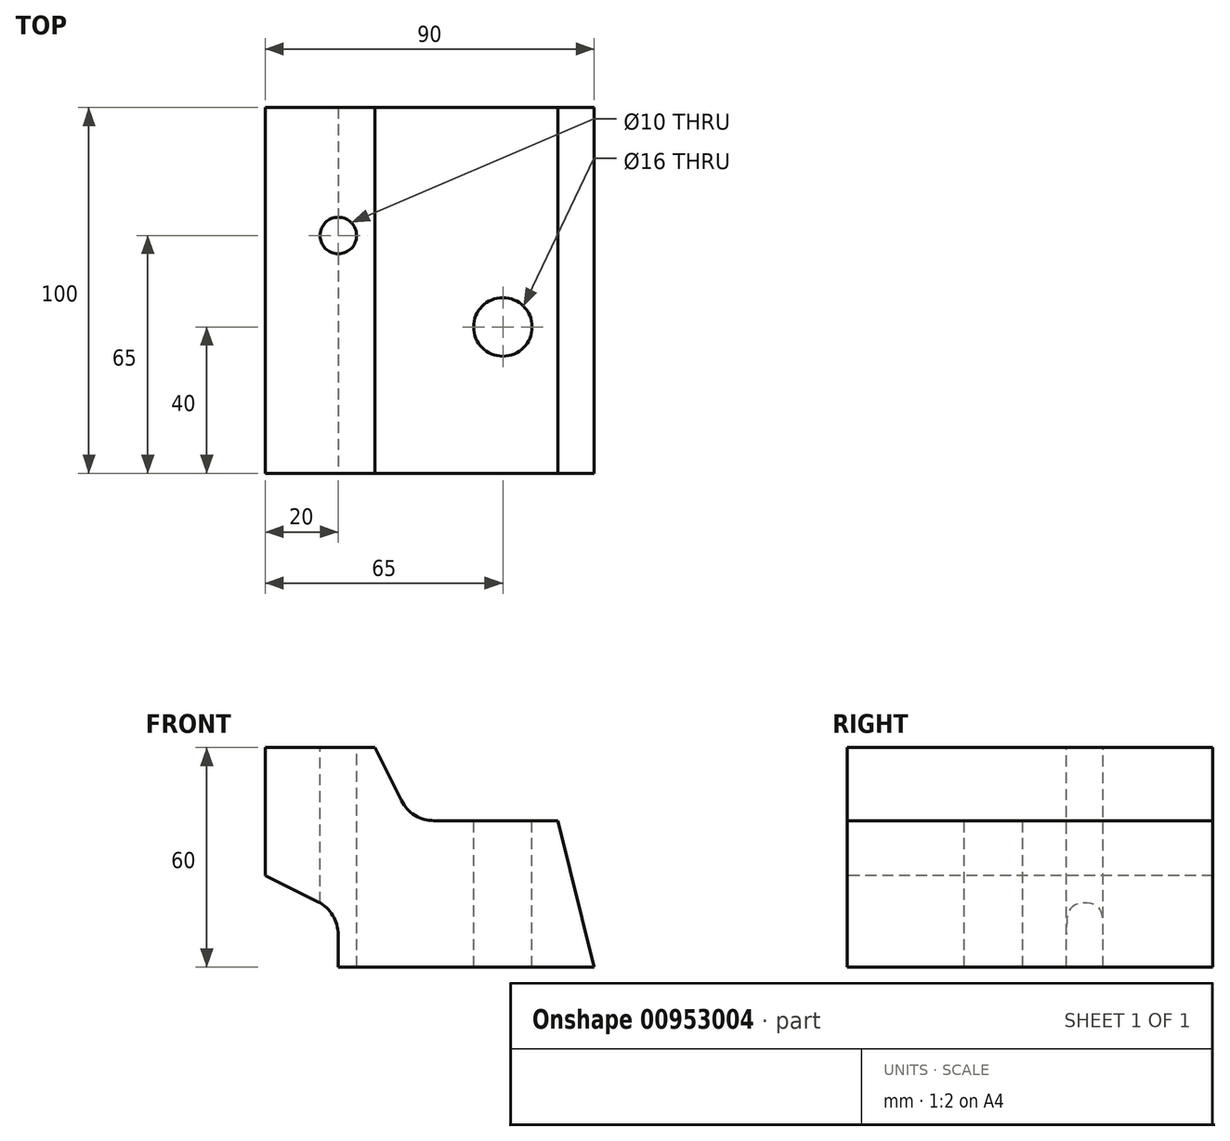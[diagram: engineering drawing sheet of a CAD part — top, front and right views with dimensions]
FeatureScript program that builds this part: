
annotation { "Feature Type Name" : "Feature", "Feature Type Description" : "" }
export const myFeature = defineFeature(function(context is Context, id is Id, definition is map)
    precondition{}
    {
        {
            var Q0;
            Q0=qCreatedBy(makeId("Front.planeOp"),FACE);
            var sketch = newSketch(context, id + "F0", { "sketchPlane" : qUnion([Q0])});
            skLineSegment(sketch, "E0", {"start": v(0, 0) * mm, "end": v(0, 15) * mm});
            skLineSegment(sketch, "E1", {"start": v(0, 15) * mm, "end": v(-20, 25) * mm});
            skLineSegment(sketch, "E2", {"start": v(-20, 25) * mm, "end": v(-20, 60) * mm});
            skLineSegment(sketch, "E3", {"start": v(-20, 60) * mm, "end": v(10, 60) * mm});
            skLineSegment(sketch, "E4", {"start": v(10, 60) * mm, "end": v(20, 40) * mm});
            skLineSegment(sketch, "E5", {"start": v(20, 40) * mm, "end": v(60, 40) * mm});
            skLineSegment(sketch, "E6", {"start": v(60, 40) * mm, "end": v(70, 0) * mm});
            skLineSegment(sketch, "E7", {"start": v(70, 0) * mm, "end": v(0, 0) * mm});
            skSolve(sketch);
        }
        {
            var Q0;
            Q0 = qSketchRegion(id + "F0", true);
            extrude(context, id + "F1", {"entities" : qUnion([Q0]), "oppositeDirection" : true, "depth" : 100 * mm, "offsetDistance" : 25 * mm});
        }
        {
            var Q0;
            Q0=makeQuery(id+"F1.opExtrude","SWEPT_EDGE",EDGE,{"disambiguationData":[OSD([sQuery(id+"F0.wireOp",EDGE,"E4"),sQuery(id+"F0.wireOp",EDGE,"E5")])]});
            var Q1;
            Q1=makeQuery(id+"F1.opExtrude","SWEPT_EDGE",EDGE,{"disambiguationData":[OSD([sQuery(id+"F0.wireOp",EDGE,"E0"),sQuery(id+"F0.wireOp",EDGE,"E1")])]});
            fillet(context, id + "F2", {"entities" : qUnion([Q0, Q1]), "radius" : 10 * mm, "tangentPropagation" : true, "allowEdgeOverflow" : false});
        }
        {
            var Q0;
            Q0=makeQuery(id+"F1.opExtrude","SWEPT_FACE",FACE,{"disambiguationData":[OSD([sQuery(id+"F0.wireOp",EDGE,"E3")])]});
            var sketch = newSketch(context, id + "F3", { "sketchPlane" : qUnion([Q0])});
            skCircle(sketch, "E8", {"center": v(0, 65) * mm, "radius": 5 * mm});
            skCircle(sketch, "E9", {"center": v(45, 40) * mm, "radius": 8 * mm});
            skSolve(sketch);
        }
        {
            var Q0;
            Q0 = qSketchRegion(id + "F3", true);
            extrude(context, id + "F4", {"entities" : qUnion([Q0]), "operationType" : NewBodyOperationType.REMOVE, "endBound" : BoundingType.THROUGH_ALL, "oppositeDirection" : true, "depth" : 25 * mm, "offsetDistance" : 25 * mm});
        }
    });
